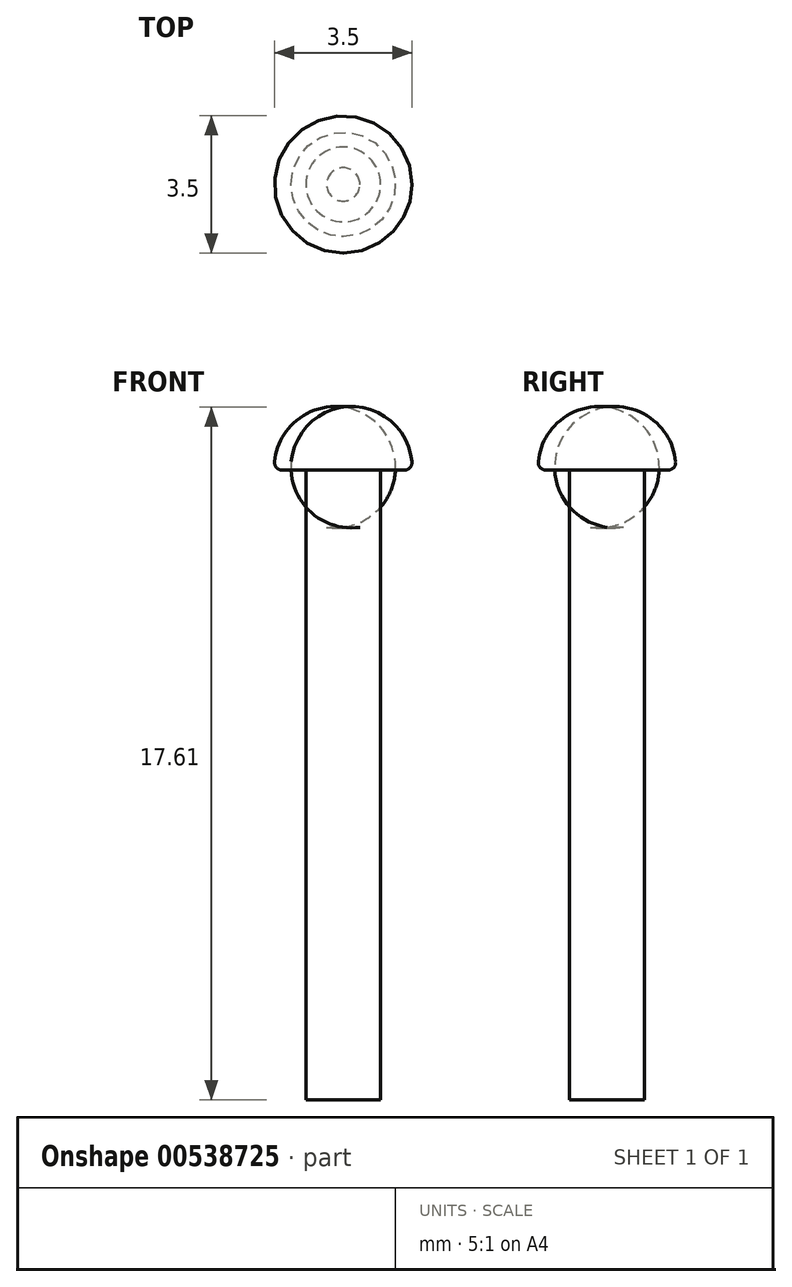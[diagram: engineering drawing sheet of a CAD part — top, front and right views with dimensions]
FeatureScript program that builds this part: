
annotation { "Feature Type Name" : "Feature", "Feature Type Description" : "" }
export const myFeature = defineFeature(function(context is Context, id is Id, definition is map)
    precondition{}
    {
        {
            var Q0;
            Q0=qCreatedBy(makeId("Front.planeOp"),FACE);
            var sketch = newSketch(context, id + "F0", { "sketchPlane" : qUnion([Q0])});
            skLineSegment(sketch, "E0", {"start": v(0, -16) * mm, "end": v(0.95, -16) * mm});
            skLineSegment(sketch, "E1", {"start": v(0.95, -16) * mm, "end": v(0.95, 0) * mm});
            skLineSegment(sketch, "E2", {"start": v(0.95, 0) * mm, "end": v(1.55, 0) * mm});
            skArc(sketch, "E3", {"start": v(1.75, 0.22) * mm, "mid": v(1.17, 1.28) * mm, "end": v(0, 1.6) * mm});
            skPoint(sketch, "E3.second.point", {"position": v(-1.16, 0.78) * mm});
            skPoint(sketch, "E3.third.point", {"position": v(0, 1.6) * mm});
            skLineSegment(sketch, "E4", {"start": v(0, 1.6) * mm, "end": v(0, -16) * mm});
            skPoint(sketch, "E5.visualSharp", {"position": v(1.75, 0) * mm});
            skArc(sketch, "E5.filletArc", {"start": v(1.55, 0) * mm, "mid": v(1.7, 0.07) * mm, "end": v(1.75, 0.22) * mm});
            skSolve(sketch);
        }
        {
            var Q0;
            Q0=makeQuery(id+"F0.imprint","IMPRINT",FACE,{"disambiguationData":[TD([[makeQuery(id+"F0.imprint","IMPRINT",EDGE,{"derivedFrom":sQuery(id+"F0.wireOp",EDGE,"E0")}),1.0]])]});
            var Q1;
            Q1=sQuery(id+"F0.wireOp",EDGE,"E4");
            revolve(context, id + "F1", {"entities" : qUnion([Q0]), "axis" : qUnion([Q1]), "revolveType" : RevolveType.FULL});
        }
    });
